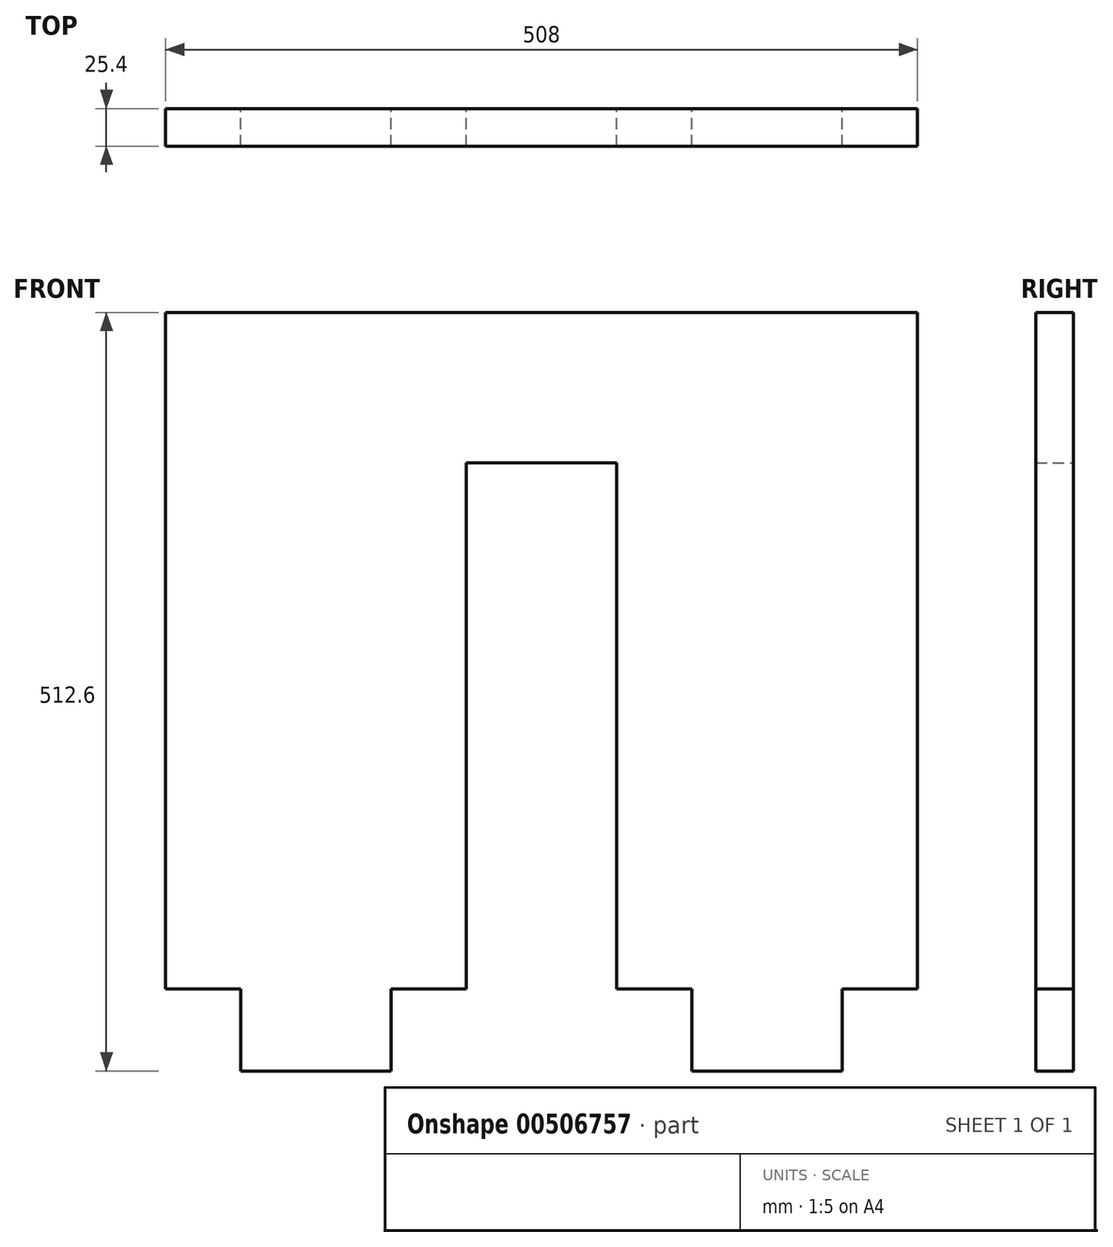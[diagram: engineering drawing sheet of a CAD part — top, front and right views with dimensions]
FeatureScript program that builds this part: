
annotation { "Feature Type Name" : "Feature", "Feature Type Description" : "" }
export const myFeature = defineFeature(function(context is Context, id is Id, definition is map)
    precondition{}
    {
        {
            var Q0;
            Q0=qCreatedBy(makeId("Front.planeOp"),FACE);
            var sketch = newSketch(context, id + "F0", { "sketchPlane" : qUnion([Q0])});
            skLineSegment(sketch, "E0", {"start": v(-134.19, 318.29) * mm, "end": v(234.73, 318.29) * mm});
            skLineSegment(sketch, "E1", {"start": v(234.73, 318.29) * mm, "end": v(234.73, -138.91) * mm});
            skLineSegment(sketch, "E2", {"start": v(234.73, -138.91) * mm, "end": v(183.93, -138.91) * mm});
            skLineSegment(sketch, "E3", {"start": v(183.93, -138.91) * mm, "end": v(183.93, -194.3) * mm});
            skLineSegment(sketch, "E4", {"start": v(183.93, -194.3) * mm, "end": v(82.33, -194.3) * mm});
            skLineSegment(sketch, "E5", {"start": v(82.33, -194.3) * mm, "end": v(82.33, -138.91) * mm});
            skLineSegment(sketch, "E6", {"start": v(82.33, -138.91) * mm, "end": v(31.53, -138.91) * mm});
            skLineSegment(sketch, "E7", {"start": v(31.53, -138.91) * mm, "end": v(31.53, 216.69) * mm});
            skLineSegment(sketch, "E8", {"start": v(31.53, 216.69) * mm, "end": v(-70.07, 216.69) * mm});
            skLineSegment(sketch, "E9", {"start": v(-70.07, 216.69) * mm, "end": v(-70.07, -138.91) * mm});
            skLineSegment(sketch, "E10", {"start": v(-70.07, -138.91) * mm, "end": v(-120.87, -138.91) * mm});
            skLineSegment(sketch, "E11", {"start": v(-120.87, -138.91) * mm, "end": v(-120.87, -194.3) * mm});
            skLineSegment(sketch, "E12", {"start": v(-120.87, -194.3) * mm, "end": v(-222.47, -194.3) * mm});
            skLineSegment(sketch, "E13", {"start": v(-222.47, -194.3) * mm, "end": v(-222.47, -138.91) * mm});
            skLineSegment(sketch, "E14", {"start": v(-222.47, -138.91) * mm, "end": v(-273.27, -138.91) * mm});
            skLineSegment(sketch, "E15", {"start": v(-273.27, -138.91) * mm, "end": v(-273.27, 318.29) * mm});
            skLineSegment(sketch, "E16", {"start": v(-273.27, 318.29) * mm, "end": v(-134.19, 318.29) * mm});
            skSolve(sketch);
        }
        {
            var Q0;
            Q0 = qSketchRegion(id + "F0", true);
            extrude(context, id + "F1", {"entities" : qUnion([Q0]), "depth" : 25.4 * mm, "offsetDistance" : 25.4 * mm});
        }
    });
